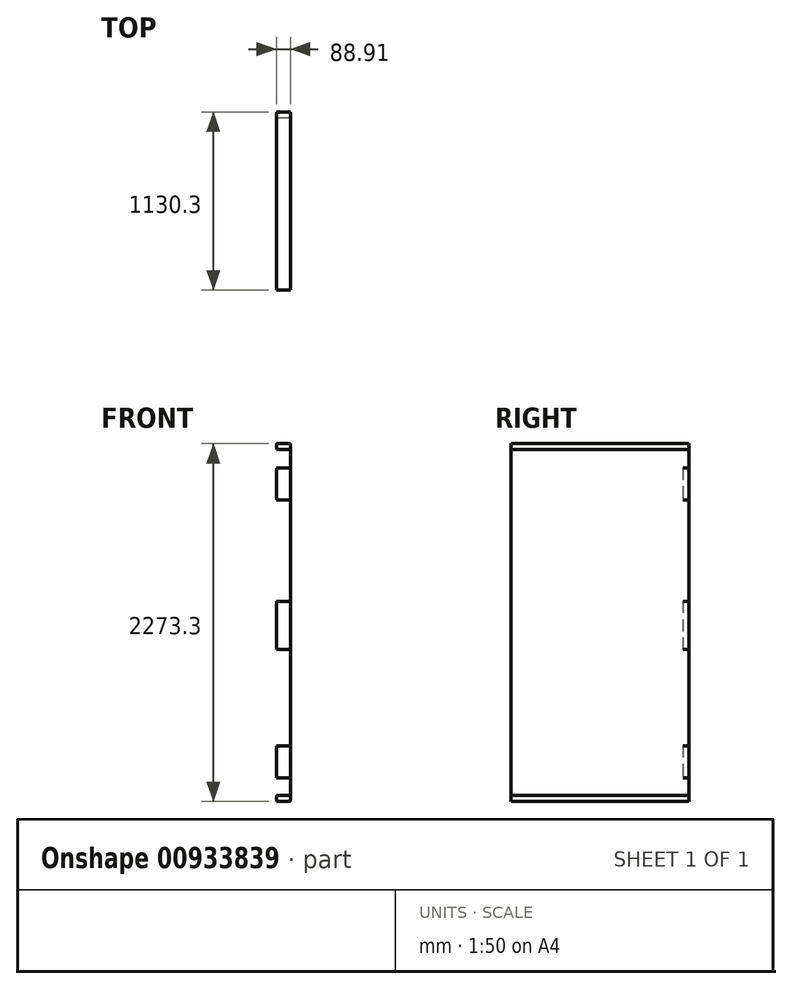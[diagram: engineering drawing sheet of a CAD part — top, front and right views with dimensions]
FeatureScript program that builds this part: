
annotation { "Feature Type Name" : "Feature", "Feature Type Description" : "" }
export const myFeature = defineFeature(function(context is Context, id is Id, definition is map)
    precondition{}
    {
        {
            var Q0;
            Q0=qCreatedBy(makeId("Right.planeOp"),FACE);
            var sketch = newSketch(context, id + "F0", { "sketchPlane" : qUnion([Q0])});
            skLineSegment(sketch, "E0.rect.bottom", {"start": v(565.15, 1136.65) * mm, "end": v(-565.15, 1136.65) * mm, "construction": true});
            skLineSegment(sketch, "E0.rect.top", {"start": v(565.15, -1136.65) * mm, "end": v(-565.15, -1136.65) * mm, "construction": true});
            skLineSegment(sketch, "E0.rect.left", {"start": v(565.15, 1136.65) * mm, "end": v(565.15, -1136.65) * mm, "construction": true});
            skLineSegment(sketch, "E0.rect.right", {"start": v(-565.15, 1136.65) * mm, "end": v(-565.15, -1136.65) * mm, "construction": true});
            skPoint(sketch, "E0.rect.middle", {"position": v(0, 0) * mm});
            skLineSegment(sketch, "E1.bottom", {"start": v(-565.15, 1136.65) * mm, "end": v(565.15, 1136.65) * mm});
            skLineSegment(sketch, "E1.top", {"start": v(-565.15, 1098.55) * mm, "end": v(565.15, 1098.55) * mm});
            skLineSegment(sketch, "E1.left", {"start": v(-565.15, 1136.65) * mm, "end": v(-565.15, 1098.55) * mm});
            skLineSegment(sketch, "E1.right", {"start": v(565.15, 1136.65) * mm, "end": v(565.15, 1098.55) * mm});
            skLineSegment(sketch, "E2", {"start": v(-565.15, 0) * mm, "end": v(565.15, 0) * mm, "construction": true});
            skLineSegment(sketch, "E3.1.MirrorCS", {"start": v(-565.15, -1098.55) * mm, "end": v(565.15, -1098.55) * mm});
            skLineSegment(sketch, "E3.2.MirrorCS", {"start": v(-565.15, -1136.65) * mm, "end": v(-565.15, -1098.55) * mm});
            skLineSegment(sketch, "E3.3.MirrorCS", {"start": v(565.15, -1136.65) * mm, "end": v(565.15, -1098.55) * mm});
            skLineSegment(sketch, "E3.4.MirrorCS", {"start": v(-565.15, -1136.65) * mm, "end": v(565.15, -1136.65) * mm});
            skLineSegment(sketch, "E4.bottom", {"start": v(-565.15, 1098.55) * mm, "end": v(-527.05, 1098.55) * mm});
            skLineSegment(sketch, "E4.top", {"start": v(-565.15, -1098.55) * mm, "end": v(-527.05, -1098.55) * mm});
            skLineSegment(sketch, "E4.left", {"start": v(-565.15, 1098.55) * mm, "end": v(-565.15, -1098.55) * mm});
            skLineSegment(sketch, "E4.right", {"start": v(-527.05, 1098.55) * mm, "end": v(-527.05, -1098.55) * mm});
            skLineSegment(sketch, "E5.0.MirrorCS", {"start": v(565.15, 1098.55) * mm, "end": v(527.05, 1098.55) * mm});
            skLineSegment(sketch, "E5.1.MirrorCS", {"start": v(565.15, -1098.55) * mm, "end": v(527.05, -1098.55) * mm});
            skLineSegment(sketch, "E6.bottom", {"start": v(565.15, 980.75) * mm, "end": v(527.05, 980.75) * mm});
            skLineSegment(sketch, "E6.top", {"start": v(565.15, 777.55) * mm, "end": v(527.05, 777.55) * mm});
            skLineSegment(sketch, "E6.left", {"start": v(565.15, 980.75) * mm, "end": v(565.15, 777.55) * mm});
            skLineSegment(sketch, "E6.right", {"start": v(527.05, 980.75) * mm, "end": v(527.05, 777.55) * mm});
            skLineSegment(sketch, "E7.bottom", {"start": v(565.15, 134.85) * mm, "end": v(527.05, 134.85) * mm});
            skLineSegment(sketch, "E7.top", {"start": v(565.15, -169.95) * mm, "end": v(527.05, -169.95) * mm});
            skLineSegment(sketch, "E7.left", {"start": v(565.15, 134.85) * mm, "end": v(565.15, -169.95) * mm});
            skLineSegment(sketch, "E7.right", {"start": v(527.05, 134.85) * mm, "end": v(527.05, -169.95) * mm});
            skLineSegment(sketch, "E8.bottom", {"start": v(565.15, -783.39) * mm, "end": v(527.05, -783.39) * mm});
            skLineSegment(sketch, "E8.top", {"start": v(565.15, -986.59) * mm, "end": v(527.05, -986.59) * mm});
            skLineSegment(sketch, "E8.left", {"start": v(565.15, -783.39) * mm, "end": v(565.15, -986.59) * mm});
            skLineSegment(sketch, "E8.right", {"start": v(527.05, -783.39) * mm, "end": v(527.05, -986.59) * mm});
            skSolve(sketch);
        }
        {
            var Q0;
            Q0=makeQuery(id+"F0.imprint","IMPRINT",FACE,{"disambiguationData":[TD([[makeQuery(id+"F0.imprint","IMPRINT",EDGE,{"derivedFrom":sQuery(id+"F0.wireOp",EDGE,"E4.bottom")}),-1.0]])]});
            var Q1;
            Q1=makeQuery(id+"F0.imprint","IMPRINT",FACE,{"disambiguationData":[TD([[makeQuery(id+"F0.imprint","IMPRINT",EDGE,{"derivedFrom":sQuery(id+"F0.wireOp",EDGE,"E5.0.MirrorCS")}),1.0]])]});
            var Q2;
            Q2=makeQuery(id+"F0.imprint","IMPRINT",FACE,{"disambiguationData":[TD([[makeQuery(id+"F0.imprint","IMPRINT",EDGE,{"derivedFrom":sQuery(id+"F0.wireOp",EDGE,"E8.bottom")}),1.0]])]});
            var Q3;
            Q3=makeQuery(id+"F0.imprint","IMPRINT",FACE,{"disambiguationData":[TD([[makeQuery(id+"F0.imprint","IMPRINT",EDGE,{"derivedFrom":sQuery(id+"F0.wireOp",EDGE,"E7.bottom")}),1.0]])]});
            var Q4;
            Q4=makeQuery(id+"F0.imprint","IMPRINT",FACE,{"disambiguationData":[TD([[makeQuery(id+"F0.imprint","IMPRINT",EDGE,{"derivedFrom":sQuery(id+"F0.wireOp",EDGE,"E6.bottom")}),1.0]])]});
            extrude(context, id + "F1", {"entities" : qUnion([Q0, Q1, Q2, Q3, Q4]), "depth" : 88.9 * mm});
        }
        {
            var Q0;
            Q0=makeQuery(id+"F0.imprint","IMPRINT",FACE,{"disambiguationData":[TD([[makeQuery(id+"F0.imprint","IMPRINT",EDGE,{"derivedFrom":sQuery(id+"F0.wireOp",EDGE,"E1.bottom")}),-1.0]])]});
            var Q1;
            Q1=makeQuery(id+"F0.imprint","IMPRINT",FACE,{"disambiguationData":[TD([[makeQuery(id+"F0.imprint","IMPRINT",EDGE,{"derivedFrom":sQuery(id+"F0.wireOp",EDGE,"E3.1.MirrorCS")}),-1.0]])]});
            extrude(context, id + "F2", {"entities" : qUnion([Q0, Q1]), "depth" : 88.9 * mm});
        }
        {
            var Q0;
            Q0=makeQuery(id+"F2.opExtrude","CAP_FACE",FACE,{"disambiguationData":[OSD([sQuery(id+"F0.wireOp",EDGE,"E1.bottom"),sQuery(id+"F0.wireOp",EDGE,"E1.top"),sQuery(id+"F0.wireOp",EDGE,"E1.left"),sQuery(id+"F0.wireOp",EDGE,"E1.right"),sQuery(id+"F0.wireOp",EDGE,"E4.bottom"),sQuery(id+"F0.wireOp",EDGE,"E5.0.MirrorCS")])],"isStart":false});
            var sketch = newSketch(context, id + "F3", { "sketchPlane" : qUnion([Q0])});
            skPoint(sketch, "E9.0", {"position": v(-565.15, 1136.65) * mm});
            skPoint(sketch, "E10.0", {"position": v(565.15, -1136.65) * mm});
            skLineSegment(sketch, "E11.bottom", {"start": v(-565.15, 1136.65) * mm, "end": v(565.15, 1136.65) * mm});
            skLineSegment(sketch, "E11.top", {"start": v(-565.15, -1136.65) * mm, "end": v(565.15, -1136.65) * mm});
            skLineSegment(sketch, "E11.left", {"start": v(-565.15, 1136.65) * mm, "end": v(-565.15, -1136.65) * mm});
            skLineSegment(sketch, "E11.right", {"start": v(565.15, 1136.65) * mm, "end": v(565.15, -1136.65) * mm});
            skSolve(sketch);
        }
        {
            var Q0;
            Q0=qSketchRegion(id+"F3",true);
            extrude(context, id + "F4", {"entities" : qUnion([Q0]), "depth" : 3 / 203.2 * mm});
        }
    });
